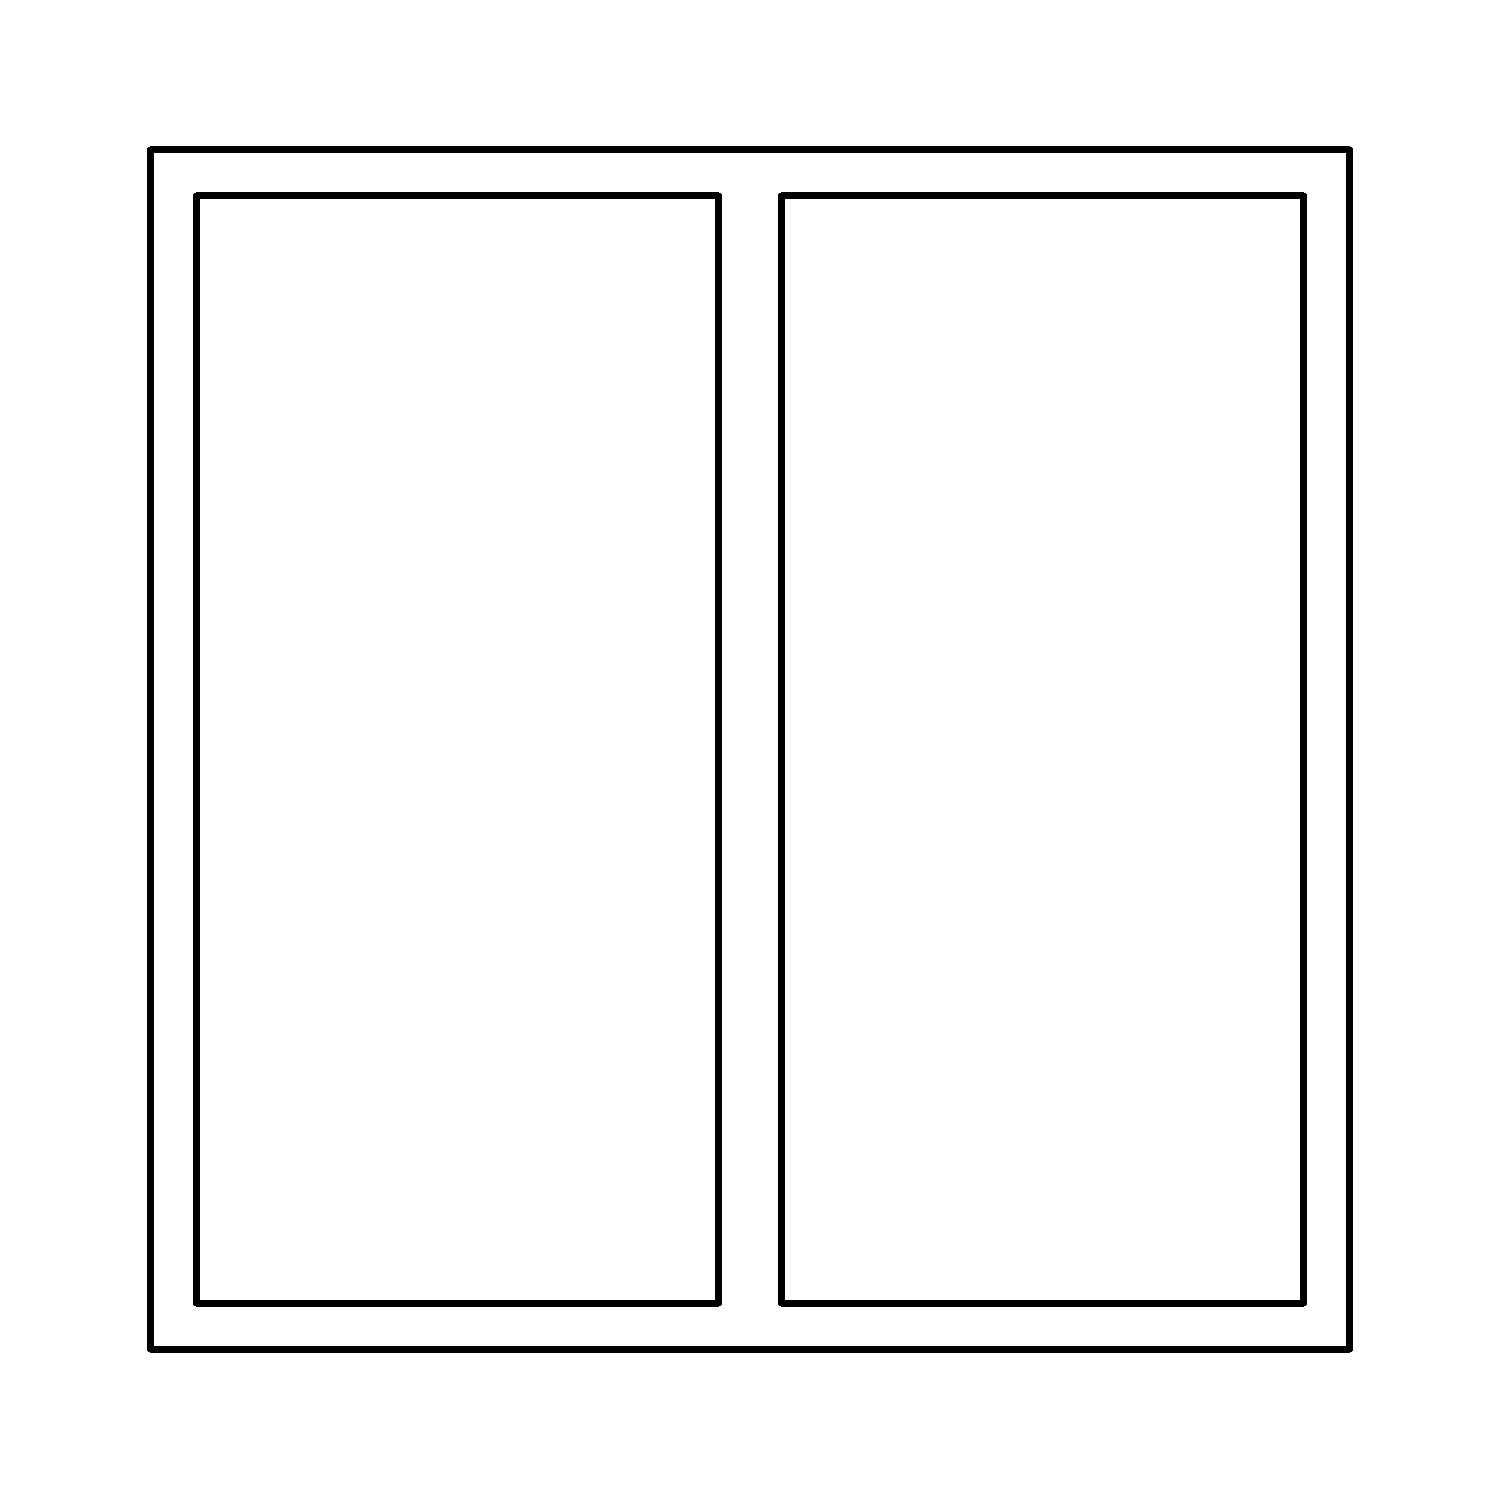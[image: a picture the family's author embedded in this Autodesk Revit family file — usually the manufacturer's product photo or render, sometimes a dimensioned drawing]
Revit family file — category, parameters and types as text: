
# Revit family: Окно.Alumark_двустворчатое_S44
name_source: partatom
category: Окна
revit_build: Autodesk Revit 2017 (Build: 20171027_0315(x64)
units: mm (PartAtom-declared; Revit-internal decimal feet)

## family parameters
Всегда вертикально = Да
Заголовок OmniClass = Windows
Номер OmniClass = 23.30.20.00
Общий = Нет
Основа = Стена
При загрузке вырезать с полостями = Нет
Точка расчета площади = Нет

## types (2) — shared parameters
#_рамы = 1000000
ADSK_Завод-изготовитель = ТБМ
ADSK_Обозначение = ГОСТ 21519-2003
URL = http://www.tbm.ru
sp_energy = Энергосберегающие стекла
sp_gaz = Заполненный газом
sp_standart = Обычный стеклопакет
Автоматический подбор рамы и створки = Да
Аналитическая конструкция = Окна с одинарным остеклением - для жилых зданий
Высота подоконника по умолчанию = 900 мм
Замыкание стены = По основе
Заполнение стеклопакета = Обычный стеклопакет
Изготовитель = ТБМ
Изображение типоразмера = схема_двупольное.png
Коэффициент теплопередачи (U) = 5.7361 Вт/(м²·K)
Коэффициент теплопритока от солнечного излучения = 0.86
Материал отлива = <По категории>
Материал подоконника = <По категории>
Материал рамы/створки = <По категории>
Материал стекла = <По категории>
Материал фурнитуры = <По категории>
Описание = Окно Проем ТБМ
Примерная высота = 1460 мм
Примерная ширина = 1460 мм
Пропускание видимого света = 0.9
Равные створки = Да
Разработчик = ООО ПРОРУБИМ
Разработчик (телефон) = +7(495)649-85-43
Створка слева = Окна.Alumark_створка_двупольная (S44) : Глухая
ТБМ_Артикул_Импост = ALM244301
ТБМ_Артикул_Клей = KMR0014
ТБМ_Артикул_Подкладка под СП = ALM740307
ТБМ_Артикул_Рама = ALM244101
ТБМ_Артикул_Распорный штифт = ALM885010
ТБМ_Артикул_Угловой соединитель рамы = ALM420011
ТБМ_Артикул_Уголок выравнивающий = ALM744014
ТБМ_Артикул_Уплотнитель внутренний = ALM770207
ТБМ_Артикул_Уплотнитель наружный = ALM770004
ТБМ_Артикул_Штапик = ALM244013
ТБМ_Длина_Импост = 1420 мм
ТБМ_Длина_Рама = 5840 мм
ТБМ_Количество_Подкладка под СП = 12
ТБМ_Количество_Угловой соединитель рамы = 4
ТБМ_Соответствие рекомендациям = Размеры окна соответствует рекомендациям компании ТБМ
ТБМ_Стеклопакет_Высота 2 = 1394 мм
ТБМ_Стеклопакет_Ширина 2 = 664 мм
Термостойкость = 0.1743 (м²·K)/Вт
Тип рамы = Рама оконная : 44/26 мм (ALM244101)
Тип створки = Створка оконная : 32/43 мм (ALM244201)
Тип стеклопакета = 16мм 1-камерный
глухая_створка = Окна.Alumark_створка_двупольная (S44) : Глухая
импост_ширина = 62 мм
обозначение_проема_высота = 243 мм
обозначение_проема_ширина = 243 мм
профиль створки_ширина = 43 мм
размер_X = 43 мм
размер_Y = 20 мм
размер_Z = 26 мм
рама_тип-1 = Рама оконная : 44/26 мм (ALM244101)
рама_тип-2 = Рама оконная : 60/42 мм (ALM244102)
рама_толщина = 44 мм
рама_ширина = 44 мм
сп_16_мм = 16мм 1-камерный
сп_24_мм = 24мм 1-камерный
створка_высота = 1372 мм
створка_слева_ширина = 655 мм
створка_справа_размер = 730 мм
створка_справа_ширина = 655 мм
створка_тип-1 = Створка оконная : 32/43 мм (ALM244201)
створка_тип-2 = Створка оконная : 48/59 мм (ALM244202)
створка_ширина = 1372 мм
таблица выбора = Каталог_окна_S44
штапик_толщина = 28 мм
штапик_ширина = 18 мм
zero-valued in all types: профиль_створка_слева_длина

## per-type parameters (varying)
- 1460х1460 (правое-откидное): #_створки=10000; ADSK_Наименование=ОАК (Профиль рамы 44/26 мм. Профиль створки 32/43 мм) СПО (Обычный стеклопакет 16 мм); Створка справа=Окна.Alumark_створка_двупольная (S44) : Правая-откидная; ТБМ_Артикул_Отлив=ALM460035-1.07; ТБМ_Артикул_Створка=ALM244201; ТБМ_Артикул_Угловой соединитель створки=ALM420011; ТБМ_Артикул_Уголок жесткости=ALM744501; ТБМ_Артикул_Уплотнитель притвора=ALM770001; ТБМ_Длина_Отлив=616 мм; ТБМ_Длина_Створка=4220 мм; ТБМ_Длина_Уплотнитель внутренний=10060 мм; ТБМ_Длина_Уплотнитель наружный=10060 мм; ТБМ_Длина_Уплотнитель притвора=4220 мм; ТБМ_Длина_Штапик=8048 мм; ТБМ_Количество_Распорный штифт=32; ТБМ_Количество_Угловой соединитель створки=4; ТБМ_Количество_Уголок выравнивающий=8; ТБМ_Количество_Уголок жесткости=4; ТБМ_Площадь стеклопакета=1.72 м²; ТБМ_Расход_Клей=96; ТБМ_Стеклопакет_Высота 1=1326 мм; ТБМ_Стеклопакет_Ширина 1=596 мм; Ширина створки справа=600 мм; номер профиля=1010101; профиль_створка_справа_длина=4220 мм
- 1460х1460 (глухое): #_створки=0; ADSK_Наименование=ОАК (Профиль рамы 44/26 мм) СПО (Обычный стеклопакет 16 мм); Створка справа=Окна.Alumark_створка_двупольная (S44) : Глухая; ТБМ_Длина_Отлив=0 мм; ТБМ_Длина_Створка=0 мм; ТБМ_Длина_Уплотнитель внутренний=11680 мм; ТБМ_Длина_Уплотнитель наружный=11680 мм; ТБМ_Длина_Уплотнитель притвора=0 мм; ТБМ_Длина_Штапик=8344 мм; ТБМ_Количество_Распорный штифт=16; ТБМ_Количество_Угловой соединитель створки=0; ТБМ_Количество_Уголок выравнивающий=4; ТБМ_Количество_Уголок жесткости=0; ТБМ_Площадь стеклопакета=1.85 м²; ТБМ_Расход_Клей=28; ТБМ_Стеклопакет_Высота 1=1394 мм; ТБМ_Стеклопакет_Ширина 1=664 мм; Ширина створки справа=0 мм; номер профиля=1000101; профиль_створка_справа_длина=0 мм
